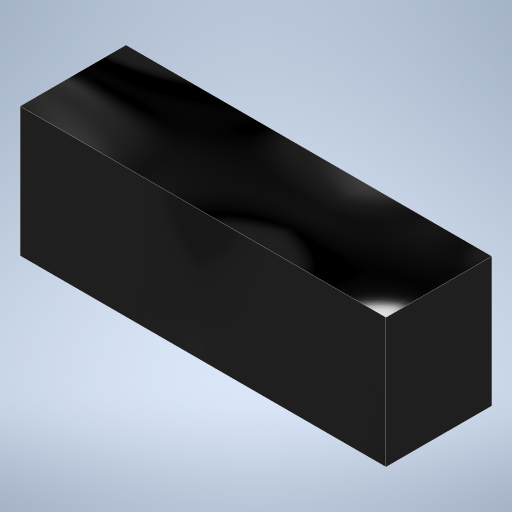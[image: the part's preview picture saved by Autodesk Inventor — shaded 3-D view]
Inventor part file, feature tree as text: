
AUTODESK INVENTOR PART (.ipt)
format: ipt  version: 2023 (Build 270158000, 158)  size: 199,168 bytes
history: native  units: in
note: dims shown in document units (in); Inventor stores cm internally (conversion verified against a paired STEP export)
features: extrude x1, sketch x1
ambient origin geometry x8: Origin, YZ Plane, XZ Plane, XY Plane, X Axis, Y Axis, Z Axis, Center Point
bodies: Solid1 (feature_tree)
feature tree (2):
  extrude  "Extrusion1"  Depth=0.112in
  sketch  "Sketch1"  dims[d0=0.387in d1=0.112in d2=0.137in d3=0.0in]
